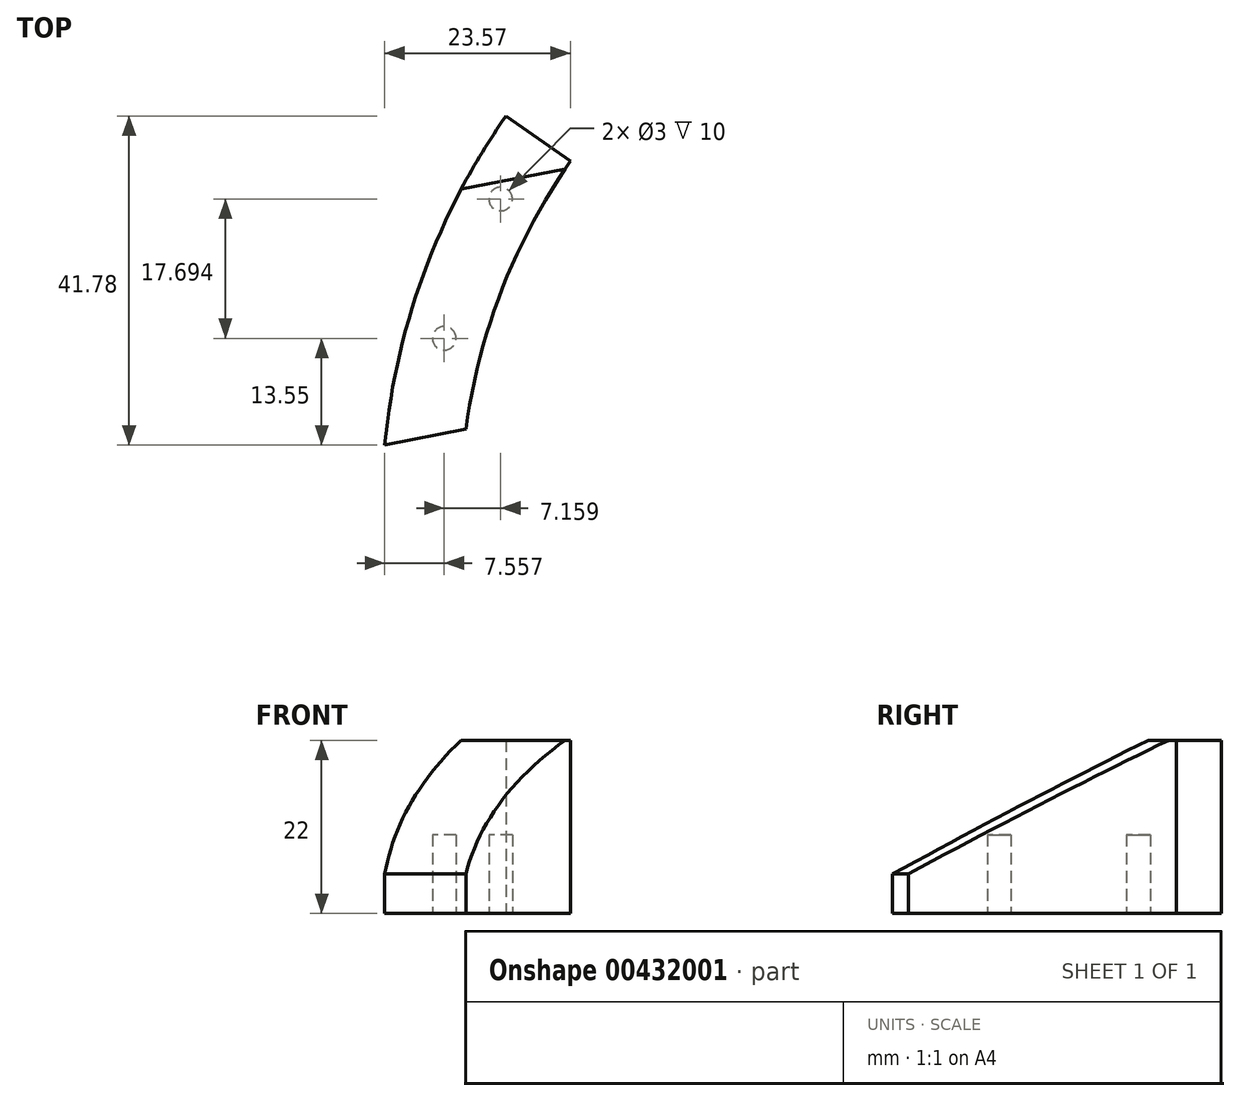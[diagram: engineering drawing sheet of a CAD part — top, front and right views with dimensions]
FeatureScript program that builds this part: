
annotation { "Feature Type Name" : "Feature", "Feature Type Description" : "" }
export const myFeature = defineFeature(function(context is Context, id is Id, definition is map)
    precondition{}
    {
        {
            var Q0;
            Q0=qCreatedBy(makeId("Top.planeOp"),FACE);
            var sketch = newSketch(context, id + "F0", { "sketchPlane" : qUnion([Q0])});
            skCircle(sketch, "E0", {"center": v(0, 0) * mm, "radius": 77.5 * mm});
            skCircle(sketch, "E1", {"center": v(0, 0) * mm, "radius": 76 * mm});
            skCircle(sketch, "E2", {"center": v(0, 0) * mm, "radius": 2.5 * mm});
            skLineSegment(sketch, "E3.bottom", {"start": v(0, 60) * mm, "end": v(-100, 60) * mm, "construction": true});
            skLineSegment(sketch, "E3.top", {"start": v(0, -60) * mm, "end": v(-100, -60) * mm, "construction": true});
            skLineSegment(sketch, "E3.left", {"start": v(0, 60) * mm, "end": v(0, -60) * mm, "construction": true});
            skLineSegment(sketch, "E3.right", {"start": v(-100, 60) * mm, "end": v(-100, -60) * mm, "construction": true});
            skCircle(sketch, "E4", {"center": v(0, 0) * mm, "radius": 87.5 * mm});
            skCircle(sketch, "E5", {"center": v(0, 0) * mm, "radius": 62.5 * mm});
            skLineSegment(sketch, "E6", {"start": v(0, 0) * mm, "end": v(-78.23, -94.42) * mm, "construction": true});
            skLineSegment(sketch, "E7", {"start": v(0, 0) * mm, "end": v(-84.15, 101.51) * mm, "construction": true});
            skLineSegment(sketch, "E8", {"start": v(0, 0) * mm, "end": v(-134.5, -26.47) * mm, "construction": true});
            skLineSegment(sketch, "E9", {"start": v(-85.85, -16.9) * mm, "end": v(-90.68, 7.63) * mm});
            skLineSegment(sketch, "E10", {"start": v(-90.68, 7.63) * mm, "end": v(-31.8, 19.22) * mm});
            skLineSegment(sketch, "E11", {"start": v(-31.8, 19.22) * mm, "end": v(-22.16, -29.84) * mm});
            skLineSegment(sketch, "E12", {"start": v(-22.16, -29.84) * mm, "end": v(-81.03, -41.42) * mm});
            skLineSegment(sketch, "E13", {"start": v(-90.68, 7.63) * mm, "end": v(-81.03, -41.42) * mm});
            skLineSegment(sketch, "E14.0", {"start": v(-84.8, 3.7) * mm, "end": v(-35.75, 13.35) * mm});
            skLineSegment(sketch, "E14.1", {"start": v(-84.8, 3.7) * mm, "end": v(-77.09, -35.55) * mm});
            skLineSegment(sketch, "E14.2", {"start": v(-28.03, -25.9) * mm, "end": v(-77.09, -35.55) * mm});
            skLineSegment(sketch, "E14.3", {"start": v(-35.75, 13.35) * mm, "end": v(-28.03, -25.9) * mm});
            skLineSegment(sketch, "E15.0", {"start": v(-94.2, 10) * mm, "end": v(-29.45, 22.74) * mm});
            skLineSegment(sketch, "E15.1", {"start": v(-94.2, 10) * mm, "end": v(-83.4, -44.95) * mm});
            skLineSegment(sketch, "E15.2", {"start": v(-18.63, -32.2) * mm, "end": v(-83.4, -44.95) * mm});
            skLineSegment(sketch, "E15.3", {"start": v(-29.45, 22.74) * mm, "end": v(-18.63, -32.2) * mm});
            skLineSegment(sketch, "E16", {"start": v(0, 0) * mm, "end": v(-75.25, 10.67) * mm, "construction": true});
            skLineSegment(sketch, "E17", {"start": v(-75.25, 10.67) * mm, "end": v(-86.63, 12.29) * mm});
            skLineSegment(sketch, "E18", {"start": v(-55.84, 67.36) * mm, "end": v(-48.5, 58.5) * mm});
            skLineSegment(sketch, "E19", {"start": v(0, 0) * mm, "end": v(-95.1, 62.97) * mm, "construction": true});
            skLineSegment(sketch, "E20", {"start": v(-72.96, 48.3) * mm, "end": v(-64.62, 42.79) * mm});
            skLineSegment(sketch, "E21", {"start": v(0, 0) * mm, "end": v(-81.95, 67.9) * mm, "construction": true});
            skLineSegment(sketch, "E22", {"start": v(-67.38, 55.83) * mm, "end": v(-59.68, 49.45) * mm});
            skLineSegment(sketch, "E23", {"start": v(0, 0) * mm, "end": v(-91.99, 64.28) * mm, "construction": true});
            skLineSegment(sketch, "E24", {"start": v(-63.53, 44.4) * mm, "end": v(-71.72, 50.12) * mm});
            skCircle(sketch, "E25", {"center": v(0, 0) * mm, "radius": 82.5 * mm, "construction": true});
            skCircle(sketch, "E26", {"center": v(-72.38, 39.58) * mm, "radius": 1.5 * mm});
            skCircle(sketch, "E27", {"center": v(-79.54, 21.89) * mm, "radius": 1.5 * mm});
            skSolve(sketch);
        }
        {
            var Q0;
            {var subQ0=sQuery(id+"F0.wireOp",EDGE,"E15.0");var subQ1=sQuery(id+"F0.wireOp",EDGE,"E0");var subQ2=makeQuery(id+"F0.imprint","INTERSECT",VERTEX,{"derivedFrom":[subQ1,subQ0]});Q0=makeQuery(id+"F0.imprint","IMPRINT",FACE,{"disambiguationData":[TD([[makeQuery(id+"F0.imprint","IMPRINT",EDGE,{"disambiguationData":[TD([[subQ2,-1.0]])],"derivedFrom":subQ1}),-1.0]])]});}
            var Q1;
            {var subQ5=sQuery(id+"F0.wireOp",EDGE,"E20");Q1=makeQuery(id+"F0.imprint","IMPRINT",FACE,{"disambiguationData":[TD([[makeQuery(id+"F0.imprint","IMPRINT",EDGE,{"derivedFrom":subQ5}),-1.0]])]});}
            var Q2;
            {var subQ0=sQuery(id+"F0.wireOp",EDGE,"E20");Q2=makeQuery(id+"F0.imprint","IMPRINT",FACE,{"disambiguationData":[TD([[makeQuery(id+"F0.imprint","IMPRINT",EDGE,{"derivedFrom":subQ0}),1.0]])]});}
            var Q3;
            {var subQ3=sQuery(id+"F0.wireOp",EDGE,"E17");var subQ7=sQuery(id+"F0.wireOp",EDGE,"E0");var subQ9=makeQuery(id+"F0.imprint","INTERSECT",VERTEX,{"derivedFrom":[subQ7,subQ3]});Q3=makeQuery(id+"F0.imprint","IMPRINT",FACE,{"disambiguationData":[TD([[makeQuery(id+"F0.imprint","IMPRINT",EDGE,{"disambiguationData":[TD([[subQ9,-1.0]])],"derivedFrom":subQ7}),-1.0]])]});}
            var Q4;
            {var subQ0=sQuery(id+"F0.wireOp",EDGE,"E17");var subQ1=sQuery(id+"F0.wireOp",EDGE,"E4");var subQ2=makeQuery(id+"F0.imprint","INTERSECT",VERTEX,{"derivedFrom":[subQ1,subQ0]});Q4=makeQuery(id+"F0.imprint","IMPRINT",FACE,{"disambiguationData":[TD([[makeQuery(id+"F0.imprint","IMPRINT",EDGE,{"disambiguationData":[TD([[subQ2,-1.0]])],"derivedFrom":subQ1}),1.0]])]});}
            var Q5;
            Q5=makeQuery(id+"F0.imprint","IMPRINT",FACE,{"disambiguationData":[TD([[makeQuery(id+"F0.imprint","IMPRINT",EDGE,{"derivedFrom":sQuery(id+"F0.wireOp",EDGE,"E26")}),1.0]])]});
            var Q6;
            Q6=makeQuery(id+"F0.imprint","IMPRINT",FACE,{"disambiguationData":[TD([[makeQuery(id+"F0.imprint","IMPRINT",EDGE,{"derivedFrom":sQuery(id+"F0.wireOp",EDGE,"E27")}),1.0]])]});
            extrude(context, id + "F1", {"entities" : qUnion([Q0, Q1, Q2, Q3, Q4, Q5, Q6]), "depth" : 22 * mm, "offsetDistance" : 25 * mm});
        }
        {
            var Q0;
            Q0=makeQuery(id+"F1.opExtrude","CAP_EDGE",EDGE,{"disambiguationData":[OSD([sQuery(id+"F0.wireOp",EDGE,"E17")])],"isStart":false});
            var Q1;
            Q1=makeQuery(id+"F1.opExtrude","CAP_EDGE",EDGE,{"disambiguationData":[OSD([sQuery(id+"F0.wireOp",EDGE,"E10")])],"isStart":false});
            chamfer(context, id + "F2", {"entities" : qUnion([Q0, Q1]), "chamferType" : ChamferType.TWO_OFFSETS, "width1" : 17 * mm, "oppositeDirection" : true, "width2" : 30 * mm, "tangentPropagation" : true});
        }
        {
            var Q0;
            Q0=makeQuery(id+"F0.imprint","IMPRINT",FACE,{"disambiguationData":[TD([[makeQuery(id+"F0.imprint","IMPRINT",EDGE,{"derivedFrom":sQuery(id+"F0.wireOp",EDGE,"E26")}),1.0]])]});
            var Q1;
            Q1=makeQuery(id+"F0.imprint","IMPRINT",FACE,{"disambiguationData":[TD([[makeQuery(id+"F0.imprint","IMPRINT",EDGE,{"derivedFrom":sQuery(id+"F0.wireOp",EDGE,"E27")}),1.0]])]});
            extrude(context, id + "F3", {"entities" : qUnion([Q0, Q1]), "operationType" : NewBodyOperationType.REMOVE, "depth" : 10 * mm, "offsetDistance" : 25 * mm});
        }
    });
